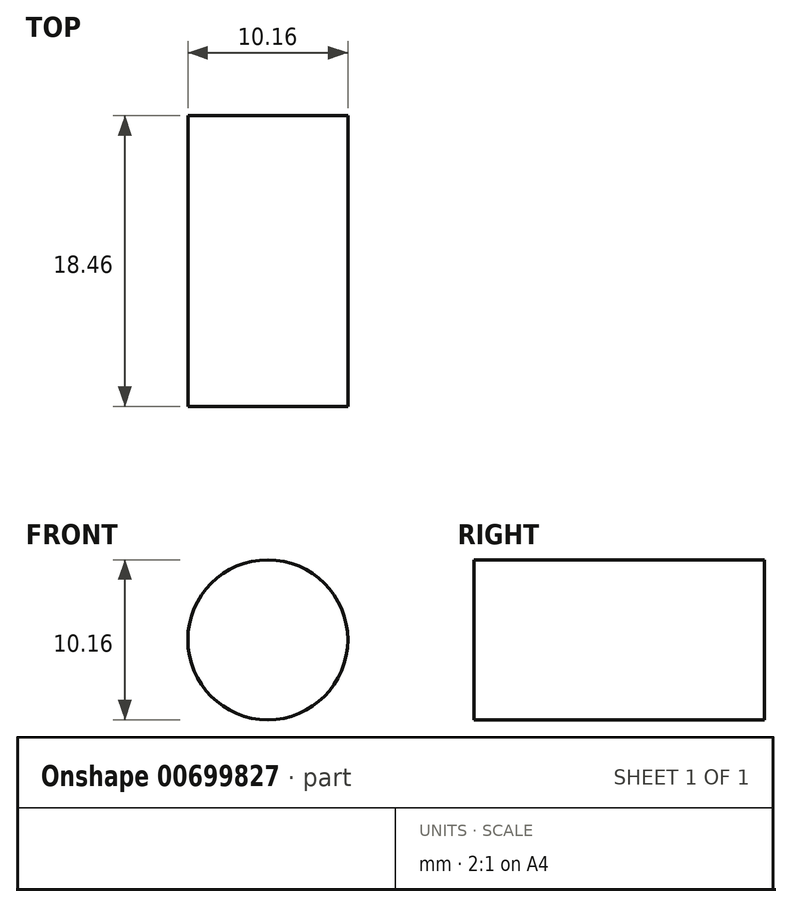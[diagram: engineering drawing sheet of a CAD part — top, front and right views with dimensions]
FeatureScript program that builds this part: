
annotation { "Feature Type Name" : "Feature", "Feature Type Description" : "" }
export const myFeature = defineFeature(function(context is Context, id is Id, definition is map)
    precondition{}
    {
        {
            var Q0;
            Q0=qCreatedBy(makeId("Front.planeOp"),FACE);
            var sketch = newSketch(context, id + "F0", { "sketchPlane" : qUnion([Q0])});
            skCircle(sketch, "E0", {"center": v(0, 0) * mm, "radius": 5.08 * mm});
            skSolve(sketch);
        }
        {
            var Q0;
            Q0=qSketchRegion(id+"F0",true);
            extrude(context, id + "F1", {"entities" : qUnion([Q0]), "depth" : 18.46 * mm});
        }
    });
